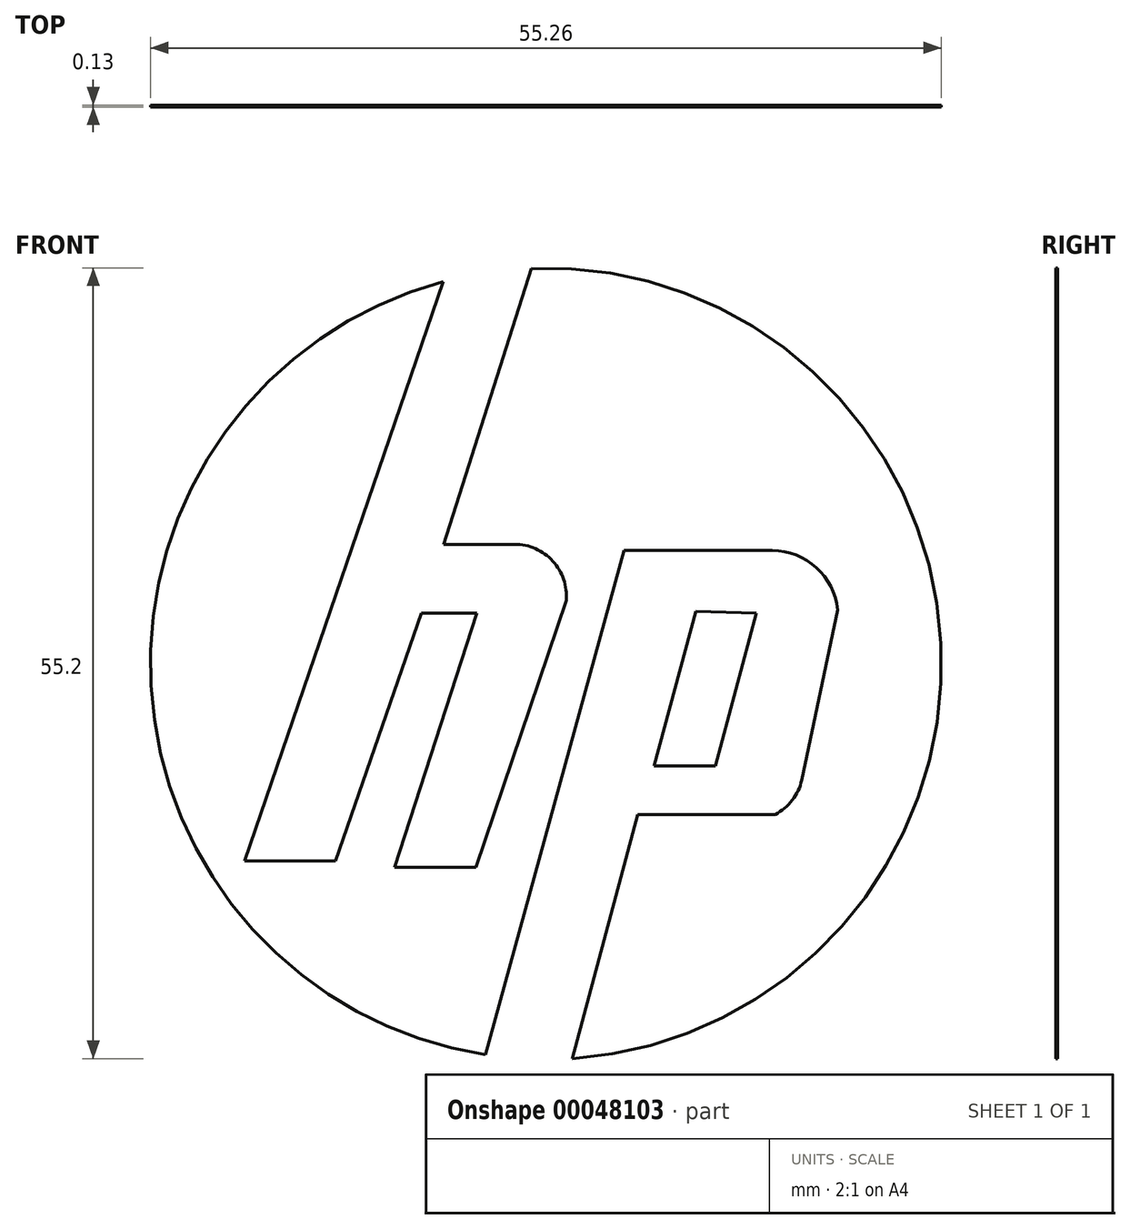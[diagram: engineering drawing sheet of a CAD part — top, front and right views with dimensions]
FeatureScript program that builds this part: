
annotation { "Feature Type Name" : "Feature", "Feature Type Description" : "" }
export const myFeature = defineFeature(function(context is Context, id is Id, definition is map)
    precondition{}
    {
        {
            var Q0;
            Q0=qCreatedBy(makeId("Front.planeOp"),FACE);
            var sketch = newSketch(context, id + "F0", { "sketchPlane" : qUnion([Q0])});
            skLineSegment(sketch, "E0", {"start": v(-14.7, -13.79) * mm, "end": v(-21.03, -13.79) * mm});
            skLineSegment(sketch, "E1", {"start": v(-21.03, -13.79) * mm, "end": v(-7.16, 26.68) * mm});
            skLineSegment(sketch, "E2", {"start": v(-4.9, -14.22) * mm, "end": v(-10.57, -14.22) * mm});
            skLineSegment(sketch, "E3", {"start": v(-10.57, -14.22) * mm, "end": v(-4.81, 3.54) * mm});
            skLineSegment(sketch, "E4", {"start": v(-4.81, 3.54) * mm, "end": v(-8.7, 3.54) * mm});
            skPoint(sketch, "E5.1.internal.snap0", {"position": v(-7.15, 8.34) * mm});
            skLineSegment(sketch, "E6", {"start": v(-7.15, 8.34) * mm, "end": v(-2.18, 8.34) * mm});
            skArc(sketch, "E7", {"start": v(-2.18, 8.34) * mm, "mid": v(0.48, 7.17) * mm, "end": v(1.42, 4.41) * mm});
            skLineSegment(sketch, "E8", {"start": v(-4.9, -14.22) * mm, "end": v(1.42, 4.41) * mm});
            skLineSegment(sketch, "E9", {"start": v(-14.7, -13.79) * mm, "end": v(-8.7, 3.54) * mm});
            skLineSegment(sketch, "E10", {"start": v(-7.15, 8.34) * mm, "end": v(-1.03, 27.61) * mm});
            skLineSegment(sketch, "E11", {"start": v(-4.21, -27.3) * mm, "end": v(5.45, 7.9) * mm});
            skLineSegment(sketch, "E12", {"start": v(5.45, 7.9) * mm, "end": v(15.8, 7.9) * mm});
            skArc(sketch, "E13", {"start": v(15.8, 7.9) * mm, "mid": v(18.89, 6.71) * mm, "end": v(20.38, 3.76) * mm});
            skLineSegment(sketch, "E14", {"start": v(20.38, 3.76) * mm, "end": v(17.87, -8.12) * mm});
            skArc(sketch, "E15", {"start": v(17.87, -8.12) * mm, "mid": v(17.22, -9.53) * mm, "end": v(16.02, -10.52) * mm});
            skLineSegment(sketch, "E16", {"start": v(16.02, -10.52) * mm, "end": v(6.43, -10.52) * mm});
            skLineSegment(sketch, "E17", {"start": v(6.43, -10.52) * mm, "end": v(1.85, -27.57) * mm});
            skLineSegment(sketch, "E18", {"start": v(14.71, 3.54) * mm, "end": v(11.84, -7.14) * mm});
            skLineSegment(sketch, "E19", {"start": v(11.84, -7.14) * mm, "end": v(7.56, -7.14) * mm});
            skLineSegment(sketch, "E20", {"start": v(7.56, -7.14) * mm, "end": v(10.46, 3.65) * mm});
            skLineSegment(sketch, "E21", {"start": v(10.46, 3.65) * mm, "end": v(14.71, 3.54) * mm});
            skArc(sketch, "E22", {"start": v(1.85, -27.57) * mm, "mid": v(27.6, 1.44) * mm, "end": v(-1.03, 27.61) * mm});
            skArc(sketch, "E23", {"start": v(-7.16, 26.68) * mm, "mid": v(-27.59, -1.5) * mm, "end": v(-4.21, -27.3) * mm});
            skSolve(sketch);
        }
        {
            var Q0;
            Q0 = qSketchRegion(id + "F0", true);
            extrude(context, id + "F1", {"entities" : qUnion([Q0]), "depth" : 0.13 * mm});
        }
    });
